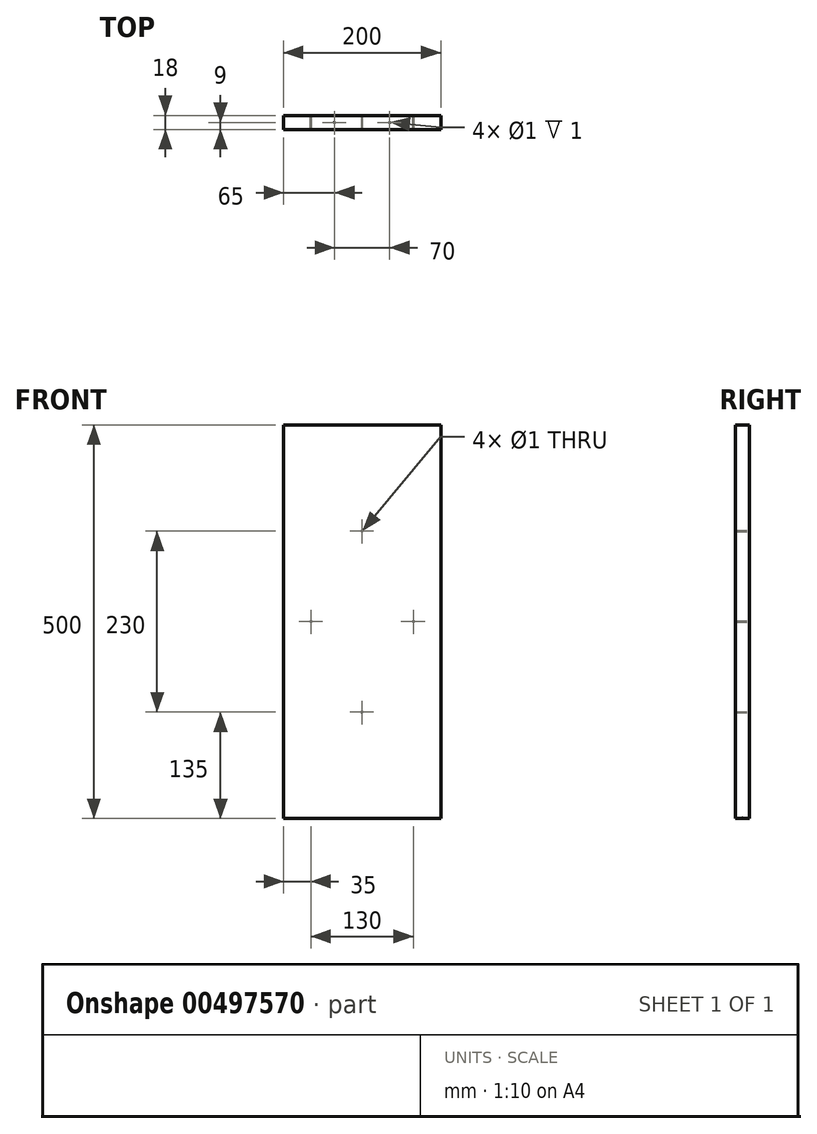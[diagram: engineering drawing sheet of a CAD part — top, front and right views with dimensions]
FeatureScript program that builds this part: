
annotation { "Feature Type Name" : "Feature", "Feature Type Description" : "" }
export const myFeature = defineFeature(function(context is Context, id is Id, definition is map)
    precondition{}
    {
        {
            var Q0;
            Q0=qCreatedBy(makeId("Front.planeOp"),FACE);
            var sketch = newSketch(context, id + "F0", { "sketchPlane" : qUnion([Q0])});
            skLineSegment(sketch, "E0.bottom", {"start": v(0, 500) * mm, "end": v(200, 500) * mm});
            skLineSegment(sketch, "E0.top", {"start": v(0, 0) * mm, "end": v(200, 0) * mm});
            skLineSegment(sketch, "E0.left", {"start": v(0, 500) * mm, "end": v(0, 0) * mm});
            skLineSegment(sketch, "E0.right", {"start": v(200, 500) * mm, "end": v(200, 0) * mm});
            skCircle(sketch, "E1", {"center": v(100, 365) * mm, "radius": 0.5 * mm});
            skLineSegment(sketch, "E2", {"start": v(0, 250) * mm, "end": v(200, 250) * mm, "construction": true});
            skCircle(sketch, "E3.MirrorC", {"center": v(100, 135) * mm, "radius": 0.5 * mm});
            skLineSegment(sketch, "E4", {"start": v(100, 500) * mm, "end": v(100, 0) * mm, "construction": true});
            skCircle(sketch, "E5", {"center": v(35, 250) * mm, "radius": 0.5 * mm});
            skCircle(sketch, "E6.MirrorC", {"center": v(165, 250) * mm, "radius": 0.5 * mm});
            skSolve(sketch);
        }
        {
            var Q0;
            Q0=makeQuery(id+"F0.imprint","IMPRINT",FACE,{"disambiguationData":[TD([[makeQuery(id+"F0.imprint","IMPRINT",EDGE,{"derivedFrom":sQuery(id+"F0.wireOp",EDGE,"E0.bottom")}),-1.0]])]});
            extrude(context, id + "F1", {"entities" : qUnion([Q0]), "depth" : 18 * mm});
        }
        {
            var Q0;
            Q0=makeQuery(id+"F1.opExtrude","SWEPT_FACE",FACE,{"disambiguationData":[OSD([sQuery(id+"F0.wireOp",EDGE,"E0.bottom")])]});
            var sketch = newSketch(context, id + "F2", { "sketchPlane" : qUnion([Q0])});
            skLineSegment(sketch, "E7", {"start": v(100, 0) * mm, "end": v(100, -18) * mm, "construction": true});
            skCircle(sketch, "E8", {"center": v(65, -9) * mm, "radius": 0.5 * mm});
            skPoint(sketch, "E8.centerSnap0", {"position": v(100, -9) * mm});
            skCircle(sketch, "E9.MirrorC", {"center": v(135, -9) * mm, "radius": 0.5 * mm});
            skSolve(sketch);
        }
        {
            var Q0;
            Q0 = qSketchRegion(id + "F2", true);
            extrude(context, id + "F3", {"entities" : qUnion([Q0]), "operationType" : NewBodyOperationType.REMOVE, "oppositeDirection" : true, "depth" : 1 * mm});
        }
        {
            var Q0;
            Q0=makeQuery(id+"F1.opExtrude","SWEPT_FACE",FACE,{"disambiguationData":[OSD([sQuery(id+"F0.wireOp",EDGE,"E0.top")])]});
            var sketch = newSketch(context, id + "F4", { "sketchPlane" : qUnion([Q0])});
            skLineSegment(sketch, "E10", {"start": v(100, 18) * mm, "end": v(100, 0) * mm, "construction": true});
            skCircle(sketch, "E11", {"center": v(65, 9) * mm, "radius": 0.5 * mm});
            skPoint(sketch, "E11.centerSnap0", {"position": v(100, 9) * mm});
            skCircle(sketch, "E12.MirrorC", {"center": v(135, 9) * mm, "radius": 0.5 * mm});
            skSolve(sketch);
        }
        {
            var Q0;
            Q0 = qSketchRegion(id + "F4", true);
            extrude(context, id + "F5", {"entities" : qUnion([Q0]), "operationType" : NewBodyOperationType.REMOVE, "oppositeDirection" : true, "depth" : 1 * mm});
        }
    });
